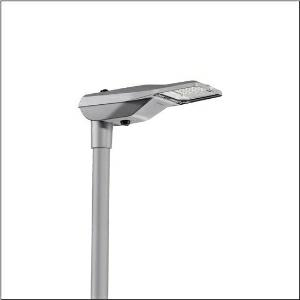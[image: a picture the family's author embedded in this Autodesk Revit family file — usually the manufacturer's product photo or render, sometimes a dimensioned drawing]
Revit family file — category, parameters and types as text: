
# Revit family: streetlight_sl_21_micro___st1_0a_5xe1d33t08db_ddb2
name_source: partatom
category: Lighting Fixtures
units: mm (PartAtom-declared; Revit-internal decimal feet)

## family parameters
Cut with Voids When Loaded = No
Host = Face
Light Source = No
Part Type = Normal
Room Calculation Point = No
Round Connector Dimension = Use Diameter
Shared = No

## types (1)
- --- (1 x LED, 5110 lm, 39.1 W, 3000K)
    Apparent Load = 39 VA
    CIE Flux Codes = 37 72 97 100 100
    Color Rendering = 70
    Color Temperature = 3000K
    Default Elevation = 1800 mm
    Description = Streetlight SL 21 micro, mast luminaire, primary light control with lens, of PMMA, primary optical cover: cover, of toughened safety glass, transparent, light distribution: ST1.0a, light emission: direct distribution, primary light characteristic: asymmetric, installation type: side-entry, post-top, LED, High Power LED, rated luminous flux: 5.110lm, luminous efficacy: 131lm/W, light colour: 730, colour temperature: 3000K, control gear: D4i, control: flexible luminous flux parameterisation, time-dependent luminous flux control, constant luminous flux control, overheat protection, pre-setting: logarithmic dimming characteristic, mains connection: 220..240V, AC, 50/60Hz, start of lifetime: 39W, end of service life: 41W, reduction: 18W, luminaire housing, of diecast aluminium, powder-coated, Siteco® metallic grey (DB 702S), corrosivity category C5 mid according to DIN EN ISO 12944, please order mast flange separately, inclination adjustable: 0°, 5°, 10°, 15°, sealing non-destructively replaceable, multi-level sealing system, length: 528mm, width: 235mm, height: 110mm, mast flange for spigot size: 42mm (side-entry): 5XC10008XM4, 60/48mm (side-entry/post-top): 5XC10108XM2, 76/60mm (side-entry/post-top): 5XC10108XM1, Smart Interface below and above, protection rating (complete): IP66, insulation class (complete): insulation class II (safety insulation), certification: CE, ENEC, ENEC+, VDE, impact resistance: IK10, permissible operating ambient temperature for outdoor applications: -40..+50°C, standard-compliant lighting for roads and squares, packaging unit: 1 piece

Light Distribution: ST1.0a
    Height = 110 mm
    Lamp = 1 x LED
    Lamp Light Flux = 5110 lm
    Lamp Power = 39.1 W
    Lamp count = 1
    Length = 528 mm
    Luminous efficacy = 131 lm/W
    Manufacturer = Siteco
    ModVariant = No
    Model = 5XE1D33T08DB
    Number of Poles = 1
    OnlyDefault = Yes
    Power Factor = 1
    Product Name = Streetlight SL 21 micro | ST1.0a
    Product group = mast luminaire | pylon top
    ProductGroupID = 6100
    Protection Class = Protection class II
    Protection Degree = IP 66
    RLX_Detail_Level = 1
    RLX_Emergency_Light_Flux = 0 lm
    RLX_Emergency_Type = 0
    RLX_Emergency_Type_DB = No
    RlxData = <blob elided: 98341 chars, md5=5cf499e4>
    Socket = socket
    Standby Power = 0 W
    System Light Flux = 5110 lm
    System Power = 39 W
    Type Comments = factory setting: luminous flux: 100 % | dim-lin: 254 | 765 mA
    Type Image = l_1007239.jpg
    URL = http://relux.com
    VarID = @adj_155798
    Voltage = 0 V
    Weight = 0.00 kg
    Width = 235 mm

## geometry (parser evidence)
native form markers: Blend x4, Sweep x11
no freeform markers — native parametric forms only
